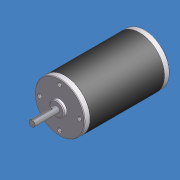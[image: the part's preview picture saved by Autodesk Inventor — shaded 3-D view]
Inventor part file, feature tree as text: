
AUTODESK INVENTOR PART (.ipt)
format: ipt  version: 2012 (Build 160160000, 160)  size: 189,952 bytes
history: native  units: mm (DEFAULTED — no unit token found)
features: sketch x9, extrude x7, chamfer x4, hole x2, pattern_circular x2, fillet x2
ambient origin geometry x8: Origin, YZ Plane, XZ Plane, XY Plane, X Axis, Y Axis, Z Axis, Center Point
bodies: Solid1 (feature_tree)
feature tree (26):
  extrude  "Extrusion1"  Depth=7.0mm TaperAngle=0.0deg
  extrude  "Extrusion2"  Depth=3.9878mm TaperAngle=0.0deg
  chamfer  "Chamfer1"  Distance=1.0mm
  hole  "Hole2"  [1 undecoded]
  pattern_circular  "Circular Pattern2"  Count=4 Angle=90.0deg
  chamfer  "Chamfer3"  Distance=31.623mm
  extrude  "Extrusion3"  Depth=12.7mm
  fillet  "Fillet1"  Radius=2.0mm
  extrude  "Extrusion4"  Depth=25.6286mm TaperAngle=0.0deg
  extrude  "Extrusion5"  Depth=95.6056mm TaperAngle=0.0deg
  extrude  "Extrusion6"  Depth=7.0mm TaperAngle=0.0deg
  extrude  "Extrusion7"  Depth=4.1148mm TaperAngle=0.0deg
  hole  "Hole3"  [1 undecoded]
  chamfer  "Chamfer2"  Distance=0.762mm
  pattern_circular  "Circular Pattern3"  [2 undecoded]
  fillet  "Fillet2"  Radius=20.0mm
  chamfer  "Chamfer4"  Distance=0.25mm
  sketch  "Sketch1"  dims[d0=64.008mm d1=7.0mm d2=0.0mm]
  sketch  "Sketch2"  dims[d3=19.05mm d4=3.9878mm d5=0.0mm d6=1.0mm d7=1.0mm]
  sketch  "Sketch4"  dims[d18=3.9624mm d19=9.525mm d20=6.35mm d21=60.0deg d22=19.05mm d23=20.594885mm d24=25.4mm d25=40.0mm d27=90.0deg]
  sketch  "Sketch5"  dims[d28=7.9502mm d29=31.623mm d30=0.0mm]
  sketch  "Sketch7"  dims[d31=0.79375mm d33=12.7mm d34=2.0mm]
  sketch  "Sketch8"  dims[d35=3.0mm d36=25.6286mm d37=0.0mm]
  sketch  "Sketch9"  dims[d38=64.4144mm d39=95.6056mm d40=0.0mm]
  sketch  "Sketch10"  dims[d41=64.008mm d42=7.0mm d43=0.0mm]
  sketch  "Sketch11"  dims[d44=30.1498mm d45=4.1148mm d46=0.0mm d47=5.08mm d48=12.7mm d49=9.906mm d50=4.572mm d51=14.3117mm d52=7.62mm d53=20.594885mm d54=0.508mm d55=3.175mm d56=0.762mm d57=0.762mm d58=3.175mm d59=20.0mm d61=360.0deg d62=0.25mm d63=3.175mm d64=45.0deg d65=45.0deg d66=45.0deg d67=45.0deg]
note: 4 required parameter values undecoded (feature->parameter linkage not recoverable at this tier; creation-order binding heuristic only, values carry confidence <= 0.55)
